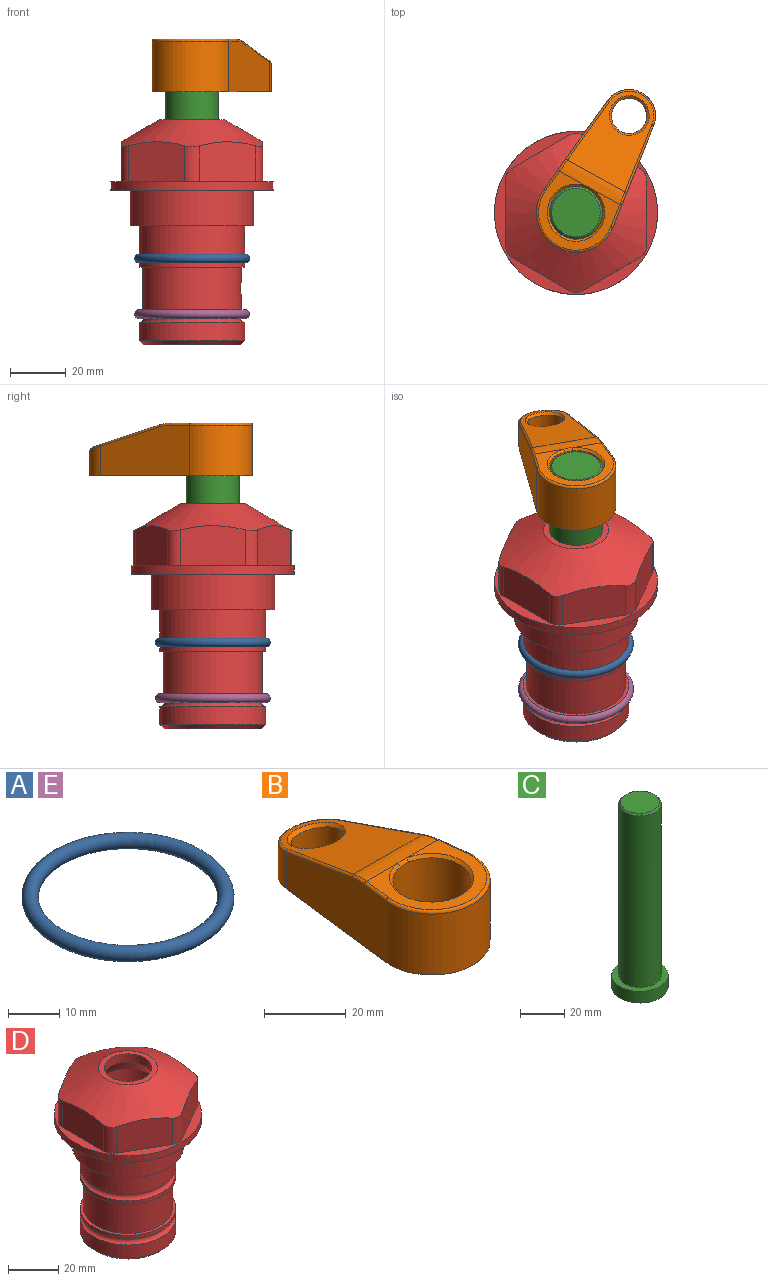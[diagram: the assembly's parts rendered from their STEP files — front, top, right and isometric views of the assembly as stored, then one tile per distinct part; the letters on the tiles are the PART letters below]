
ASSEMBLY  parts=5 mates=4
PART A: 1 faces, bbox 44.7x44.7x3.2 mm
  f0: torus R=19.05mm, axis (0,0,1), area 1193.9mm2
PART B: 31 faces, bbox 31.7x65.5x19.8 mm
  f0: plane 39.12x18.26mm, normal (0.99,0.12,0), area 612.2mm2, adj f1,f4,f7,f11,f13,f15
  f1: cylinder r=9.53mm len=18.91mm, axis (0,0,-1), area 296.1mm2, adj f0,f2,f7,f17
  f2: plane 39.12x18.26mm, normal (-0.99,0.12,0), area 612.2mm2, adj f1,f4,f7,f12,f14,f16
  f3: cylinder r=6.35mm len=12.7mm, axis (0,0,-1), area 362.4mm2, adj f7,f18
  f4: cylinder r=14.29mm len=28.58mm, axis (0,0,-1), area 882.2mm2, adj f0,f2,f7,f10
  f5: cylinder r=9.53mm len=19.05mm, axis (0,0,-1), area 1092.6mm2, adj f7,f19,f20
  f6: plane 26.99x23.69mm, normal (0,0,1), area 216.2mm2, adj f9,f10,f11,f12,f19
  f7: plane 63.5x28.58mm, normal (0,0,-1), area 661.8mm2, adj f0,f1,f2,f3,f4,f5,f22,f23
  f8: plane 33.52x23.6mm, normal (0,0.26,0.97), area 486mm2, adj f9,f15,f16,f17,f18
  f9: cylinder r=19.05mm len=24.72mm, axis (1,0,0), area 120.4mm2, adj f6,f8,f13,f14,f20
  f10: torus R=13.49mm, axis (0,0,1), area 59mm2, adj f4,f6,f11,f12
  f11: cylinder r=0.79mm len=8.67mm, axis (0.12,-0.99,0), area 10.8mm2, adj f0,f6,f10,f13
  f12: cylinder r=0.79mm len=8.67mm, axis (0.12,0.99,0), area 10.8mm2, adj f2,f6,f10,f14
  f13: bspline ~4.95x1.42mm, area 6.1mm2, adj f0,f9,f11,f15
  f14: bspline ~4.95x1.42mm, area 6.1mm2, adj f2,f9,f12,f16
  f15: cylinder r=0.79mm len=25.95mm, axis (0.12,-0.96,0.26), area 32.9mm2, adj f0,f8,f13,f17
  f16: cylinder r=0.79mm len=25.95mm, axis (0.12,0.96,-0.26), area 32.9mm2, adj f2,f8,f14,f17
  f17: bspline ~18.91x8.38mm, area 30mm2, adj f1,f8,f15,f16
  f18: bspline ~14.29x14.29mm, area 48.3mm2, adj f3,f8
  f19: cone r=9.53mm half-angle=45deg, axis (0,0,1), area 66.5mm2, adj f5,f6,f20
  f20: bspline ~3.22x0.96mm, area 3.5mm2, adj f5,f9,f19
  f21: plane 2.75x2.72mm, normal (0,0,-1), area 2.9mm2, adj f23,f25,f28
  f22: plane 23.05x15.88mm, normal (-0.99,-0.12,0), area 323.6mm2, adj f7,f25,f26,f27,f28,f29
  f23: plane 23.05x15.88mm, normal (0.99,-0.12,0), area 323.6mm2, adj f7,f21,f25,f27,f28,f30
  f24: cylinder r=9.53mm len=10.69mm, axis (0,0,-1), area 114.7mm2, adj f7,f27,f29,f30
  f25: cylinder r=12.7mm len=20.59mm, axis (0,0,-1), area 381.1mm2, adj f7,f21,f22,f23,f26,f28
  f26: plane 2.75x2.72mm, normal (0,0,-1), area 2.9mm2, adj f22,f25,f28
  f27: plane 19.72x18.37mm, normal (0,-0.26,-0.97), area 291.8mm2, adj f22,f23,f24,f28,f29,f30
  f28: cylinder r=15.88mm len=19.92mm, axis (1,0,0), area 54.8mm2, adj f21,f22,f23,f25,f26,f27
  f29: cylinder r=1.59mm len=11mm, axis (0,0,-1), area 34.7mm2, adj f7,f22,f24,f27
  f30: cylinder r=1.59mm len=11mm, axis (0,0,-1), area 34.7mm2, adj f7,f23,f24,f27
PART C: 6 faces, bbox 25.4x25.4x101.6 mm
  f0: plane 17.46x17.46mm, normal (0,0,1), area 239.5mm2, adj f5
  f1: plane 25.4x25.4mm, normal (0,0,-1), area 506.7mm2, adj f2
  f2: cylinder r=12.7mm len=25.4mm, axis (0,0,1), area 506.7mm2, adj f1,f3
  f3: plane 25.4x25.4mm, normal (0,0,1), area 221.7mm2, adj f2,f4
  f4: cylinder r=9.53mm len=94.46mm, axis (0,0,1), area 5653mm2, adj f3,f5
  f5: cone r=8.73mm half-angle=45deg, axis (0,0,-1), area 64.4mm2, adj f0,f4
PART D: 36 faces, bbox 58.7x58.7x81 mm
  f0: cylinder r=17.78mm len=35.56mm, axis (0,0,1), area 1670.8mm2, adj f23,f24,f31
  f1: cylinder r=19.05mm len=38.1mm, axis (0,0,1), area 1191.9mm2, adj f26,f27,f30
  f2: plane 58.66x58.66mm, normal (0,0,-1), area 1150.6mm2, adj f3,f28
  f3: cylinder r=29.33mm len=58.66mm, axis (0,0,-1), area 585.1mm2, adj f2,f4
  f4: plane 58.66x58.66mm, normal (0,0,1), area 475.9mm2, adj f3,f5,f6,f7,f8,f9,f10,f11
  f5: plane 20.32x14.34mm, normal (-0.5,0.87,0), area 324.4mm2, adj f4,f15,f16,f17
  f6: plane 20.32x14.34mm, normal (0.5,0.87,0), area 324.4mm2, adj f4,f14,f15,f17
  f7: plane 23.48x14.34mm, normal (1,0,0), area 324.4mm2, adj f4,f13,f14,f17
  f8: plane 20.32x14.34mm, normal (0.5,-0.87,0), area 324.4mm2, adj f4,f12,f13,f17
  f9: plane 20.32x14.34mm, normal (-0.5,-0.87,0), area 324.4mm2, adj f4,f11,f12,f17
  f10: plane 23.48x14.34mm, normal (-1,0,0), area 324.4mm2, adj f4,f11,f16,f17
  f11: cylinder r=5.08mm len=12.85mm, axis (0,0,-1), area 67.2mm2, adj f4,f9,f10,f17
  f12: cylinder r=5.08mm len=12.85mm, axis (0,0,-1), area 67.2mm2, adj f4,f8,f9,f17
  f13: cylinder r=5.08mm len=12.85mm, axis (0,0,-1), area 67.2mm2, adj f4,f7,f8,f17
  f14: cylinder r=5.08mm len=12.85mm, axis (0,0,-1), area 67.2mm2, adj f4,f6,f7,f17
  f15: cylinder r=5.08mm len=12.85mm, axis (0,0,-1), area 67.2mm2, adj f4,f5,f6,f17
  f16: cylinder r=5.08mm len=12.85mm, axis (0,0,-1), area 67.2mm2, adj f4,f5,f10,f17
  f17: cone r=11.73mm half-angle=60deg, axis (0,0,-1), area 2071.8mm2, adj f5,f6,f7,f8,f9,f10,f11,f12
  f18: plane 23.46x23.46mm, normal (0,0,1), area 147.4mm2, adj f17,f35
  f19: plane 34.93x34.93mm, normal (0,0,-1), area 958mm2, adj f29
  f20: cylinder r=19.05mm len=38.1mm, axis (0,0,1), area 760.1mm2, adj f21,f29
  f21: torus R=19.05mm, axis (0,0,1), area 565.3mm2, adj f20,f22
  f22: cylinder r=19.05mm len=38.1mm, axis (0,0,1), area 190mm2, adj f21,f23
  f23: plane 38.1x38.1mm, normal (0,0,1), area 146.9mm2, adj f0,f22
  f24: plane 38.1x38.1mm, normal (0,0,-1), area 146.9mm2, adj f0,f25
  f25: cylinder r=19.05mm len=38.1mm, axis (0,0,1), area 190mm2, adj f24,f26
  f26: torus R=19.05mm, axis (0,0,1), area 565.3mm2, adj f1,f25
  f27: plane 44.45x44.45mm, normal (0,0,-1), area 411.7mm2, adj f1,f28
  f28: cylinder r=22.23mm len=44.45mm, axis (0,0,1), area 1773.5mm2, adj f2,f27
  f29: cone r=19.05mm half-angle=45deg, axis (0,0,1), area 257.5mm2, adj f19,f20
  f30: cylinder r=3.17mm len=6.75mm, axis (-1,0,0), area 128mm2, adj f1,f33
  f31: cylinder r=3.17mm len=6.35mm, axis (-1,0,0), area 102.5mm2, adj f0,f33
  f32: plane 25.4x25.4mm, normal (0,0,1), area 506.7mm2, adj f33
  f33: cylinder r=12.7mm len=66.42mm, axis (0,0,-1), area 5236.2mm2, adj f30,f31,f32,f34
  f34: cone r=9.53mm half-angle=30deg, axis (0,0,-1), area 443.4mm2, adj f33,f35
  f35: cylinder r=9.53mm len=19.05mm, axis (0,0,-1), area 240.9mm2, adj f18,f34
PART E: same geometry as A
PLACE A at identity
PLACE B rot(axis=(0,0,-1),28.8deg) t=(0,0,-9.06)mm
PLACE C rot(axis=(0,0,-1),28.8deg) t=(0,0,-9.86)mm
PLACE D at identity fixed
PLACE E t=(0,0,-20)mm
MATE fastened E.f0 <-> D.f0  axis (0,0,1) through (0,0,-44.51)mm
MATE fastened A.f0 <-> D.f0  axis (0,0,1) through (0,0,-24.51)mm
MATE cylindrical C.f2 <-> D.f0  axis (0,0,-1) through (0,0,-47.96)mm
MATE fastened C.f2 <-> B.f4  axis (0,0,1) through (0,0,53.64)mm
